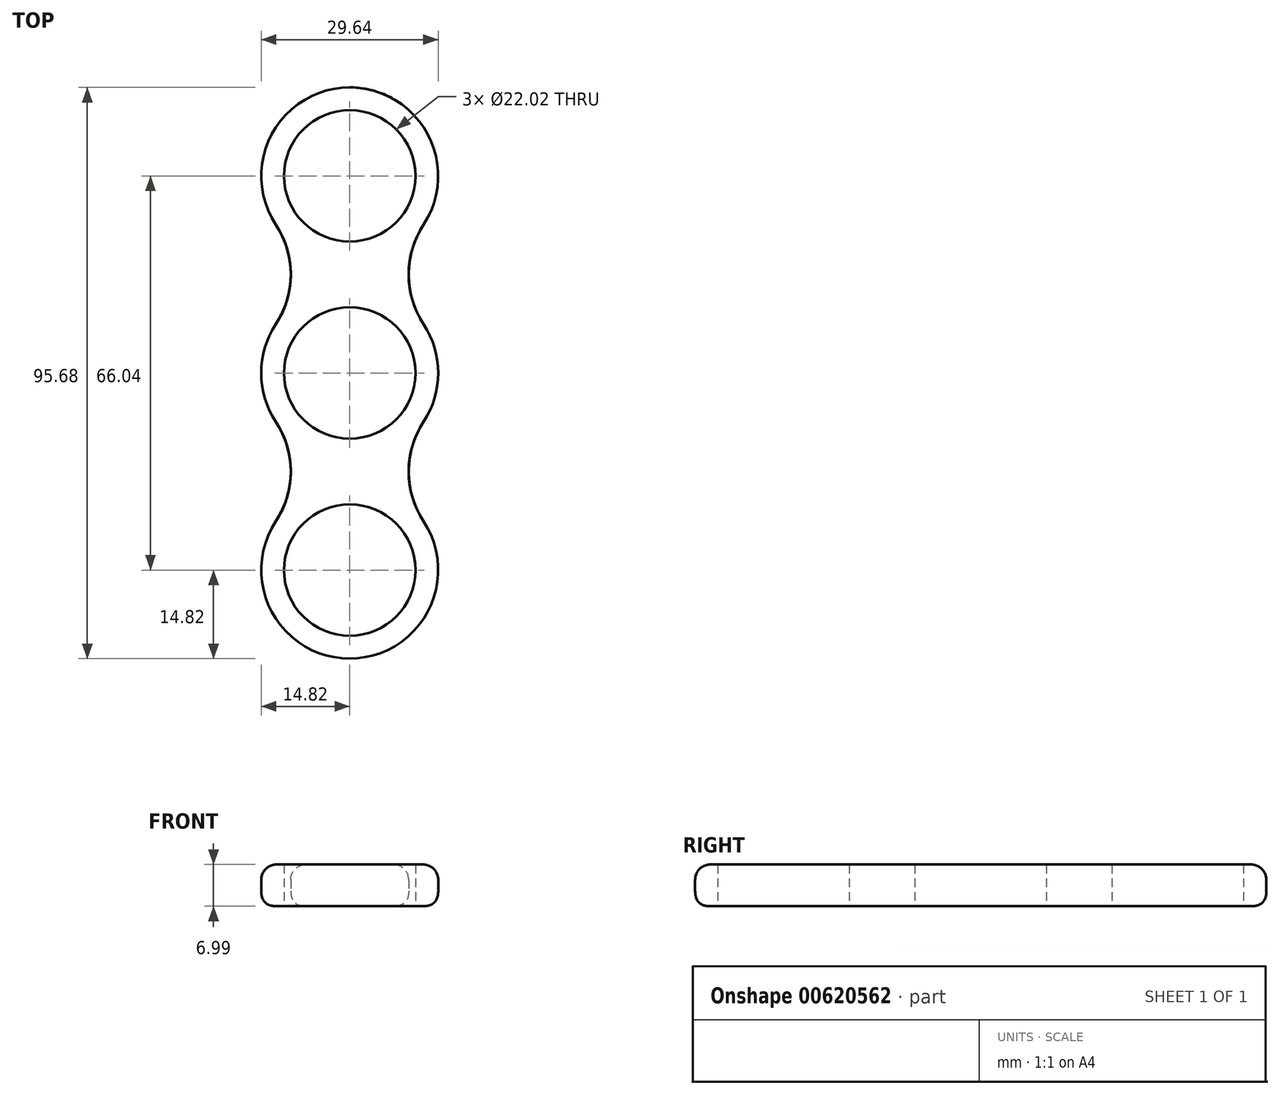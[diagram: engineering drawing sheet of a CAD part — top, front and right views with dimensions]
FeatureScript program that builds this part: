
annotation { "Feature Type Name" : "Feature", "Feature Type Description" : "" }
export const myFeature = defineFeature(function(context is Context, id is Id, definition is map)
    precondition{}
    {
        {
            var Q0;
            Q0=qCreatedBy(makeId("Top.planeOp"),FACE);
            var sketch = newSketch(context, id + "F0", { "sketchPlane" : qUnion([Q0])});
            skCircle(sketch, "E0", {"center": v(0, 0) * mm, "radius": 11.01 * mm});
            skLineSegment(sketch, "E1", {"start": v(0, 0) * mm, "end": v(0, 33.02) * mm});
            skCircle(sketch, "E2", {"center": v(0, 33.02) * mm, "radius": 11.01 * mm});
            skCircle(sketch, "E3", {"center": v(0, 33.02) * mm, "radius": 14.82 * mm});
            skCircle(sketch, "E4", {"center": v(0, 0) * mm, "radius": 14.82 * mm});
            skArc(sketch, "E5", {"start": v(-12.39, 8.14) * mm, "mid": v(-9.88, 16.51) * mm, "end": v(-12.39, 24.88) * mm});
            skArc(sketch, "E6", {"start": v(12.39, 24.88) * mm, "mid": v(9.88, 16.5) * mm, "end": v(12.39, 8.14) * mm});
            skCircle(sketch, "E7.MirrorC", {"center": v(0, -33.02) * mm, "radius": 11.01 * mm});
            skCircle(sketch, "E8.MirrorC", {"center": v(0, -33.02) * mm, "radius": 14.82 * mm});
            skArc(sketch, "E9.MirrorCS", {"start": v(-12.39, -8.14) * mm, "mid": v(-9.88, -16.51) * mm, "end": v(-12.39, -24.88) * mm});
            skArc(sketch, "E10.MirrorCS", {"start": v(12.39, -24.88) * mm, "mid": v(9.88, -16.5) * mm, "end": v(12.39, -8.14) * mm});
            skLineSegment(sketch, "E11", {"start": v(0, 0) * mm, "end": v(0, -33.02) * mm});
            skSolve(sketch);
        }
        {
            var Q0;
            Q0 = qSketchRegion(id + "F0", true);
            extrude(context, id + "F1", {"entities" : qUnion([Q0]), "depth" : 7 * mm, "offsetDistance" : 25.4 * mm});
        }
        {
            var Q0;
            Q0=makeQuery(id+"F1.opExtrude","CAP_EDGE",EDGE,{"disambiguationData":[OSD([sQuery(id+"F0.wireOp",EDGE,"E5")])],"isStart":true});
            fillet(context, id + "F2", {"entities" : qUnion([Q0]), "radius" : 2.54 * mm, "tangentPropagation" : true, "rho" : 0.5, "crossSection" : FilletCrossSection.CONIC, "allowEdgeOverflow" : false});
        }
        {
            var Q0;
            Q0=makeQuery(id+"F1.opExtrude","CAP_EDGE",EDGE,{"disambiguationData":[OSD([sQuery(id+"F0.wireOp",EDGE,"E5")])],"isStart":false});
            fillet(context, id + "F3", {"entities" : qUnion([Q0]), "radius" : 2.54 * mm, "tangentPropagation" : true, "allowEdgeOverflow" : false});
        }
    });
